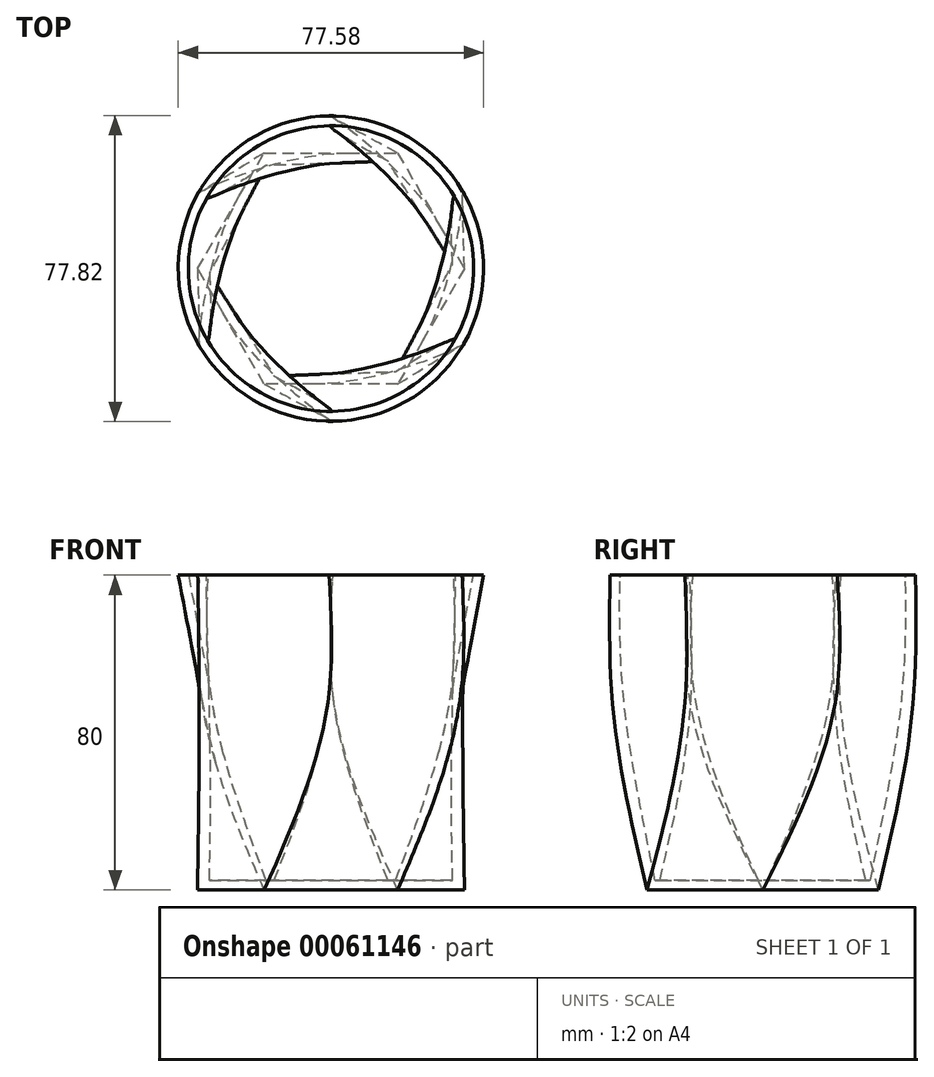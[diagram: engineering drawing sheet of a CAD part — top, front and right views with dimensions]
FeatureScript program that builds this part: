
annotation { "Feature Type Name" : "Feature", "Feature Type Description" : "" }
export const myFeature = defineFeature(function(context is Context, id is Id, definition is map)
    precondition{}
    {
        {
            var Q0;
            Q0=qCreatedBy(makeId("Top.planeOp"),FACE);
            var sketch = newSketch(context, id + "F0", { "sketchPlane" : qUnion([Q0])});
            skCircle(sketch, "E0.cCircle", {"center": v(0, 0) * mm, "radius": 29.37 * mm, "construction": true});
            skLineSegment(sketch, "E0.0", {"start": v(33.92, 0) * mm, "end": v(16.96, -29.37) * mm});
            skLineSegment(sketch, "E0.1", {"start": v(16.96, -29.37) * mm, "end": v(-16.96, -29.37) * mm});
            skLineSegment(sketch, "E0.2", {"start": v(-16.96, -29.37) * mm, "end": v(-33.92, 0) * mm});
            skLineSegment(sketch, "E0.3", {"start": v(-33.92, 0) * mm, "end": v(-16.96, 29.37) * mm});
            skLineSegment(sketch, "E0.4", {"start": v(-16.96, 29.37) * mm, "end": v(16.96, 29.37) * mm});
            skLineSegment(sketch, "E0.5", {"start": v(16.96, 29.37) * mm, "end": v(33.92, 0) * mm});
            skPoint(sketch, "E0.0.midPoint", {"position": v(25.44, -14.69) * mm});
            skSolve(sketch);
        }
        {
            var Q0;
            Q0=qCreatedBy(makeId("Top.planeOp"),FACE);
            cPlane(context, id + "F1", {"entities" : qUnion([Q0]), "cplaneType" : CPlaneType.OFFSET, "offset" : 50 * mm, "width" : 150 * mm, "height" : 150 * mm});
        }
        {
            var Q0;
            Q0=qCreatedBy(id+"F1.planeOp",FACE);
            var sketch = newSketch(context, id + "F2", { "sketchPlane" : qUnion([Q0])});
            skCircle(sketch, "E1.cCircle", {"center": v(0, 0) * mm, "radius": 33.23 * mm, "construction": true});
            skLineSegment(sketch, "E1.0", {"start": v(32.98, -19.62) * mm, "end": v(-0.5, -38.37) * mm});
            skLineSegment(sketch, "E1.1", {"start": v(-0.5, -38.37) * mm, "end": v(-33.48, -18.76) * mm});
            skLineSegment(sketch, "E1.2", {"start": v(-33.48, -18.76) * mm, "end": v(-32.98, 19.62) * mm});
            skLineSegment(sketch, "E1.3", {"start": v(-32.98, 19.62) * mm, "end": v(0.5, 38.37) * mm});
            skLineSegment(sketch, "E1.4", {"start": v(0.5, 38.37) * mm, "end": v(33.48, 18.76) * mm});
            skLineSegment(sketch, "E1.5", {"start": v(33.48, 18.76) * mm, "end": v(32.98, -19.62) * mm});
            skPoint(sketch, "E1.0.midPoint", {"position": v(16.24, -29) * mm});
            skSolve(sketch);
        }
        {
            var Q0;
            Q0=qCreatedBy(id+"F1.planeOp",FACE);
            cPlane(context, id + "F3", {"entities" : qUnion([Q0]), "cplaneType" : CPlaneType.OFFSET, "offset" : 30 * mm, "width" : 150 * mm, "height" : 150 * mm});
        }
        {
            var Q0;
            Q0=qCreatedBy(id+"F3.planeOp",FACE);
            var sketch = newSketch(context, id + "F4", { "sketchPlane" : qUnion([Q0])});
            skCircle(sketch, "E2", {"center": v(0, 0) * mm, "radius": 38.79 * mm});
            skSolve(sketch);
        }
        {
            var Q0;
            Q0=makeQuery(id+"F0.imprint","IMPRINT",FACE,{"disambiguationData":[TD([[makeQuery(id+"F0.imprint","IMPRINT",EDGE,{"derivedFrom":sQuery(id+"F0.wireOp",EDGE,"E0.0")}),-1.0]])]});
            var Q1;
            Q1=makeQuery(id+"F2.imprint","IMPRINT",FACE,{"disambiguationData":[TD([[makeQuery(id+"F2.imprint","IMPRINT",EDGE,{"derivedFrom":sQuery(id+"F2.wireOp",EDGE,"E1.0")}),-1.0]])]});
            var Q2;
            Q2=makeQuery(id+"F4.imprint","IMPRINT",FACE,{"disambiguationData":[TD([[makeQuery(id+"F4.imprint","IMPRINT",EDGE,{"derivedFrom":sQuery(id+"F4.wireOp",EDGE,"E2")}),1.0]])]});
            loft(context, id + "F5", {"sheetProfilesArray" : [{ "sheetProfileEntities" : qUnion([Q0]) }, { "sheetProfileEntities" : qUnion([Q1]) }, { "sheetProfileEntities" : qUnion([Q2]) }]});
        }
        {
            var Q0;
            Q0=makeQuery(id+"F5.opLoft","CAP_FACE",FACE,{"disambiguationData":[OSD([makeQuery(id+"F4.imprint","IMPRINT",FACE,{"disambiguationData":[TD([[makeQuery(id+"F4.imprint","IMPRINT",EDGE,{"derivedFrom":sQuery(id+"F4.wireOp",EDGE,"E2")}),1.0]])]})])],"isStart":true});
            shell(context, id + "F6", {"entities" : qUnion([Q0]), "thickness" : 2.5 * mm});
        }
    });
